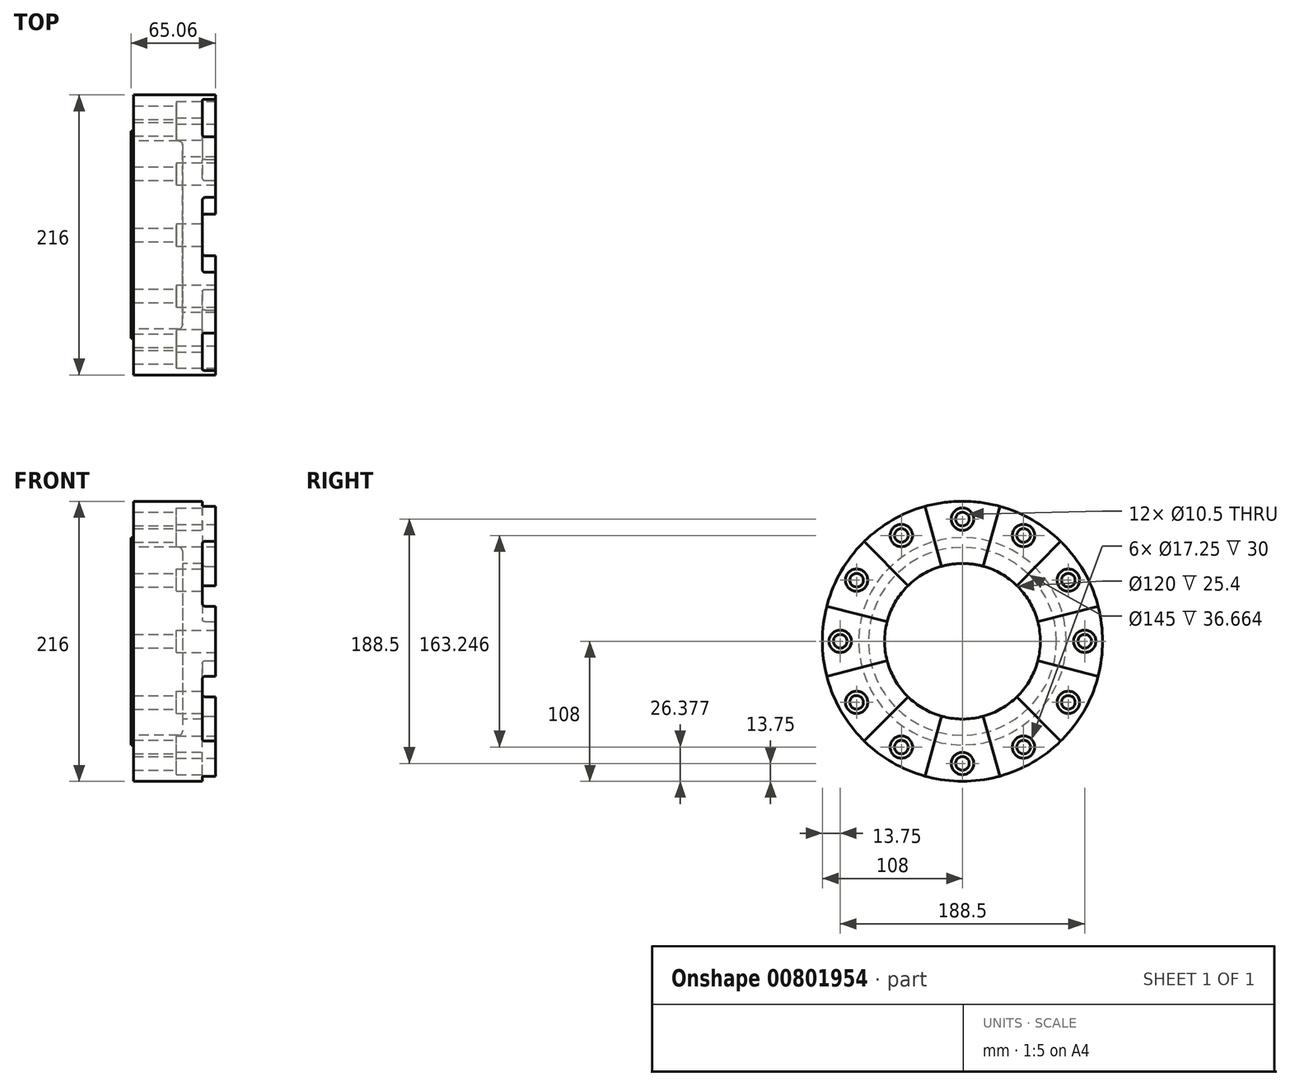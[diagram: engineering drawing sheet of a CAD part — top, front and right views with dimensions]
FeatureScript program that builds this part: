
annotation { "Feature Type Name" : "Feature", "Feature Type Description" : "" }
export const myFeature = defineFeature(function(context is Context, id is Id, definition is map)
    precondition{}
    {
        {
            var Q0;
            Q0=qCreatedBy(makeId("Front.planeOp"),FACE);
            var sketch = newSketch(context, id + "F0", { "sketchPlane" : qUnion([Q0])});
            skLineSegment(sketch, "E0", {"start": v(0, 0) * mm, "end": v(87.54, 0) * mm, "construction": true});
            skLineSegment(sketch, "E1", {"start": v(79.56, 108) * mm, "end": v(79.56, 60) * mm});
            skLineSegment(sketch, "E2", {"start": v(79.56, 60) * mm, "end": v(54.16, 60) * mm});
            skLineSegment(sketch, "E3", {"start": v(54.16, 60) * mm, "end": v(54.16, 69.5) * mm});
            skPoint(sketch, "E4.visualSharp", {"position": v(54.16, 72.5) * mm});
            skLineSegment(sketch, "E5", {"start": v(16.5, 80) * mm, "end": v(16.5, 108) * mm});
            skLineSegment(sketch, "E6", {"start": v(16.5, 108) * mm, "end": v(79.56, 108) * mm});
            skLineSegment(sketch, "E7", {"start": v(14.5, 72.5) * mm, "end": v(14.5, 80) * mm});
            skLineSegment(sketch, "E8", {"start": v(14.5, 80) * mm, "end": v(16.5, 80) * mm});
            skLineSegment(sketch, "E9", {"start": v(14.5, 72.5) * mm, "end": v(51.16, 72.5) * mm});
            skArc(sketch, "E10.filletArc", {"start": v(54.16, 69.5) * mm, "mid": v(53.29, 71.62) * mm, "end": v(51.16, 72.5) * mm});
            skSolve(sketch);
        }
        {
            var Q0;
            Q0=qSketchRegion(id+"F0",true);
            var Q1;
            Q1=sQuery(id+"F0.wireOp",EDGE,"E0");
            revolve(context, id + "F1", {"entities" : qUnion([Q0]), "axis" : qUnion([Q1]), "revolveType" : RevolveType.FULL});
        }
        {
            var Q0;
            Q0=makeQuery(id+"F1.opRevolve","SWEPT_FACE",FACE,{"disambiguationData":[OSD([sQuery(id+"F0.wireOp",EDGE,"E1")])]});
            var sketch = newSketch(context, id + "F2", { "sketchPlane" : qUnion([Q0])});
            skLineSegment(sketch, "E11", {"start": v(0, 0) * mm, "end": v(0, 110.4) * mm, "construction": true});
            skArc(sketch, "E12", {"start": v(-16.03, 57.82) * mm, "mid": v(0, 60) * mm, "end": v(16.03, 57.82) * mm});
            skArc(sketch, "E13", {"start": v(-28.86, 104.07) * mm, "mid": v(0, 108) * mm, "end": v(28.86, 104.07) * mm});
            skLineSegment(sketch, "E14", {"start": v(-28.86, 104.07) * mm, "end": v(-16.03, 57.82) * mm});
            skLineSegment(sketch, "E15", {"start": v(28.86, 104.07) * mm, "end": v(16.03, 57.82) * mm});
            skLineSegment(sketch, "E16.1.0", {"start": v(-75.7, 77.03) * mm, "end": v(-42.05, 42.8) * mm});
            skArc(sketch, "E16.1.1", {"start": v(-58.09, 15.02) * mm, "mid": v(-51.96, 30) * mm, "end": v(-42.05, 42.8) * mm});
            skArc(sketch, "E16.1.2", {"start": v(-104.56, 27.04) * mm, "mid": v(-93.53, 54) * mm, "end": v(-75.7, 77.03) * mm});
            skLineSegment(sketch, "E16.1.3", {"start": v(-104.56, 27.04) * mm, "end": v(-58.09, 15.02) * mm});
            skLineSegment(sketch, "E16.2.0", {"start": v(-104.56, -27.04) * mm, "end": v(-58.09, -15.02) * mm});
            skArc(sketch, "E16.2.1", {"start": v(-42.05, -42.8) * mm, "mid": v(-51.96, -30) * mm, "end": v(-58.09, -15.02) * mm});
            skArc(sketch, "E16.2.2", {"start": v(-75.7, -77.03) * mm, "mid": v(-93.53, -54) * mm, "end": v(-104.56, -27.04) * mm});
            skLineSegment(sketch, "E16.2.3", {"start": v(-75.7, -77.03) * mm, "end": v(-42.05, -42.8) * mm});
            skLineSegment(sketch, "E16.3.0", {"start": v(-28.86, -104.07) * mm, "end": v(-16.03, -57.82) * mm});
            skArc(sketch, "E16.3.1", {"start": v(16.03, -57.82) * mm, "mid": v(0, -60) * mm, "end": v(-16.03, -57.82) * mm});
            skArc(sketch, "E16.3.2", {"start": v(28.86, -104.07) * mm, "mid": v(0, -108) * mm, "end": v(-28.86, -104.07) * mm});
            skLineSegment(sketch, "E16.3.3", {"start": v(28.86, -104.07) * mm, "end": v(16.03, -57.82) * mm});
            skLineSegment(sketch, "E16.4.0", {"start": v(75.7, -77.03) * mm, "end": v(42.05, -42.8) * mm});
            skArc(sketch, "E16.4.1", {"start": v(58.09, -15.02) * mm, "mid": v(51.96, -30) * mm, "end": v(42.05, -42.8) * mm});
            skArc(sketch, "E16.4.2", {"start": v(104.56, -27.04) * mm, "mid": v(93.53, -54) * mm, "end": v(75.7, -77.03) * mm});
            skLineSegment(sketch, "E16.4.3", {"start": v(104.56, -27.04) * mm, "end": v(58.09, -15.02) * mm});
            skLineSegment(sketch, "E16.5.0", {"start": v(104.56, 27.04) * mm, "end": v(58.09, 15.02) * mm});
            skArc(sketch, "E16.5.1", {"start": v(42.05, 42.8) * mm, "mid": v(51.96, 30) * mm, "end": v(58.09, 15.02) * mm});
            skArc(sketch, "E16.5.2", {"start": v(75.7, 77.03) * mm, "mid": v(93.53, 54) * mm, "end": v(104.56, 27.04) * mm});
            skLineSegment(sketch, "E16.5.3", {"start": v(75.7, 77.03) * mm, "end": v(42.05, 42.8) * mm});
            skSolve(sketch);
        }
        {
            var Q0;
            Q0=qSketchRegion(id+"F2",true);
            extrude(context, id + "F3", {"entities" : qUnion([Q0]), "operationType" : NewBodyOperationType.REMOVE, "oppositeDirection" : true, "depth" : 10 * mm});
        }
        {
            var Q0;
            Q0=makeQuery(id+"F3.boolean.opBoolean","SPLIT",FACE,{"disambiguationData":[TD([makeQuery(id+"F3.opExtrude","SWEPT_FACE",FACE,{"disambiguationData":[OSD([sQuery(id+"F2.wireOp",EDGE,"E14")])]})])],"derivedFrom":makeQuery(id+"F1.opRevolve","SWEPT_FACE",FACE,{"disambiguationData":[OSD([sQuery(id+"F0.wireOp",EDGE,"E1")])]})});
            var sketch = newSketch(context, id + "F4", { "sketchPlane" : qUnion([Q0])});
            skLineSegment(sketch, "E17", {"start": v(0, 0) * mm, "end": v(0, 94.25) * mm, "construction": true});
            skCircle(sketch, "E18", {"center": v(0, 94.25) * mm, "radius": 5 * mm});
            skCircle(sketch, "E19.1.0", {"center": v(-47.12, 81.62) * mm, "radius": 5 * mm});
            skCircle(sketch, "E19.2.0", {"center": v(-81.62, 47.13) * mm, "radius": 5 * mm});
            skCircle(sketch, "E19.3.0", {"center": v(-94.25, 0) * mm, "radius": 5 * mm});
            skCircle(sketch, "E19.4.0", {"center": v(-81.62, -47.12) * mm, "radius": 5 * mm});
            skCircle(sketch, "E19.5.0", {"center": v(-47.13, -81.62) * mm, "radius": 5 * mm});
            skCircle(sketch, "E19.6.0", {"center": v(0, -94.25) * mm, "radius": 5 * mm});
            skCircle(sketch, "E19.7.0", {"center": v(47.12, -81.62) * mm, "radius": 5 * mm});
            skCircle(sketch, "E19.8.0", {"center": v(81.62, -47.13) * mm, "radius": 5 * mm});
            skCircle(sketch, "E19.9.0", {"center": v(94.25, 0) * mm, "radius": 5 * mm});
            skCircle(sketch, "E19.10.0", {"center": v(81.62, 47.12) * mm, "radius": 5 * mm});
            skCircle(sketch, "E19.11.0", {"center": v(47.12, 81.62) * mm, "radius": 5 * mm});
            skPoint(sketch, "E19.center", {"position": v(0, 0) * mm});
            skCircle(sketch, "E20", {"center": v(0, 0) * mm, "radius": 94.25 * mm, "construction": true});
            skSolve(sketch);
        }
        {
            var Q0;
            Q0=sQuery(id+"F4.wireOp",VERTEX,"E19.1.0.center");
            var Q1;
            Q1=sQuery(id+"F4.wireOp",VERTEX,"E19.3.0.center");
            var Q2;
            Q2=sQuery(id+"F4.wireOp",VERTEX,"E19.5.0.center");
            var Q3;
            Q3=sQuery(id+"F4.wireOp",VERTEX,"E19.11.0.center");
            var Q4;
            Q4=sQuery(id+"F4.wireOp",VERTEX,"E19.9.0.center");
            var Q5;
            Q5=sQuery(id+"F4.wireOp",VERTEX,"E19.7.0.center");
            var Q6;
            Q6=makeQuery(id+"F1.opRevolve","SWEPT_BODY",BODY,{"disambiguationData":[OSD([sQuery(id+"F0.wireOp",EDGE,"cKsjdh96-D89g-5p2D-h3XL-UVhXMyCSQNq4"),sQuery(id+"F0.wireOp",EDGE,"apuWihD5-RSD5-dsa5-vE7C-J3piarLAXm6q"),sQuery(id+"F0.wireOp",EDGE,"KV8aVnY1-u6Om-Dk3w-krVR-1GxTJCxTkb02"),sQuery(id+"F0.wireOp",EDGE,"Kmc8ooil-dtvY-6vtC-WxYi-Np3pAdkpifhF"),sQuery(id+"F0.wireOp",EDGE,"9beadaba-26b4-418a-b517-611681b9f9d4.filletArc"),sQuery(id+"F0.wireOp",EDGE,"E1"),sQuery(id+"F0.wireOp",EDGE,"E2"),sQuery(id+"F0.wireOp",EDGE,"E3"),sQuery(id+"F0.wireOp",EDGE,"DEHAbUA3-ssQc-y9Ke-qyxT-0Mpok7RH61FX"),sQuery(id+"F0.wireOp",EDGE,"E4.filletArc")])]});
            hole(context, id + "F5", {"style" : HoleStyle.C_BORE, "endStyle" : HoleEndStyle.THROUGH, "holeDiameter" : 10.5 * mm, "cBoreDiameter" : 17.25 * mm, "cBoreDepth" : 30 * mm, "majorDiameter" : 5 * mm, "tappedDepth" : 12 * mm, "tapClearance" : 3, "startFromSketch" : true, "locations" : qUnion([Q0, Q1, Q2, Q3, Q4, Q5]), "scope" : qUnion([Q6])});
        }
        {
            var Q0;
            Q0=makeQuery(id+"F3.boolean.opBoolean","COPY",FACE,{"derivedFrom":makeQuery(id+"F3.opExtrude","CAP_FACE",FACE,{"disambiguationData":[OSD([sQuery(id+"F2.wireOp",EDGE,"E12"),sQuery(id+"F2.wireOp",EDGE,"E13"),sQuery(id+"F2.wireOp",EDGE,"E14"),sQuery(id+"F2.wireOp",EDGE,"E15")])],"isStart":false})});
            var sketch = newSketch(context, id + "F6", { "sketchPlane" : qUnion([Q0])});
            skPoint(sketch, "E21", {"position": v(0, 94.25) * mm});
            skPoint(sketch, "E22.1.0", {"position": v(-81.62, 47.12) * mm});
            skPoint(sketch, "E22.2.0", {"position": v(-81.62, -47.12) * mm});
            skPoint(sketch, "E22.3.0", {"position": v(0, -94.25) * mm});
            skPoint(sketch, "E22.4.0", {"position": v(81.62, -47.13) * mm});
            skPoint(sketch, "E22.5.0", {"position": v(81.62, 47.12) * mm});
            skPoint(sketch, "E22.center", {"position": v(0, 0) * mm});
            skSolve(sketch);
        }
        {
            var Q0;
            Q0=sQuery(id+"F6.wireOp",VERTEX,"E21");
            var Q1;
            Q1=sQuery(id+"F6.wireOp",VERTEX,"E22.1.0");
            var Q2;
            Q2=sQuery(id+"F6.wireOp",VERTEX,"E22.2.0");
            var Q3;
            Q3=sQuery(id+"F6.wireOp",VERTEX,"E22.3.0");
            var Q4;
            Q4=sQuery(id+"F6.wireOp",VERTEX,"E22.4.0");
            var Q5;
            Q5=sQuery(id+"F6.wireOp",VERTEX,"E22.5.0");
            var Q6;
            Q6=makeQuery(id+"F1.opRevolve","SWEPT_BODY",BODY,{"disambiguationData":[OSD([sQuery(id+"F0.wireOp",EDGE,"cKsjdh96-D89g-5p2D-h3XL-UVhXMyCSQNq4"),sQuery(id+"F0.wireOp",EDGE,"apuWihD5-RSD5-dsa5-vE7C-J3piarLAXm6q"),sQuery(id+"F0.wireOp",EDGE,"KV8aVnY1-u6Om-Dk3w-krVR-1GxTJCxTkb02"),sQuery(id+"F0.wireOp",EDGE,"Kmc8ooil-dtvY-6vtC-WxYi-Np3pAdkpifhF"),sQuery(id+"F0.wireOp",EDGE,"9beadaba-26b4-418a-b517-611681b9f9d4.filletArc"),sQuery(id+"F0.wireOp",EDGE,"E1"),sQuery(id+"F0.wireOp",EDGE,"E2"),sQuery(id+"F0.wireOp",EDGE,"E3"),sQuery(id+"F0.wireOp",EDGE,"DEHAbUA3-ssQc-y9Ke-qyxT-0Mpok7RH61FX"),sQuery(id+"F0.wireOp",EDGE,"E4.filletArc")])]});
            hole(context, id + "F7", {"style" : HoleStyle.C_BORE, "endStyle" : HoleEndStyle.THROUGH, "holeDiameter" : 10.5 * mm, "cBoreDiameter" : 17.25 * mm, "cBoreDepth" : 20 * mm, "majorDiameter" : 5 * mm, "tappedDepth" : 12 * mm, "tapClearance" : 3, "startFromSketch" : true, "locations" : qUnion([Q0, Q1, Q2, Q3, Q4, Q5]), "scope" : qUnion([Q6])});
        }
        {
            var Q0;
            Q0=makeQuery(id+"F3.boolean.opBoolean","COPY",EDGE,{"derivedFrom":makeQuery(id+"F3.opExtrude","CAP_EDGE",EDGE,{"disambiguationData":[OSD([sQuery(id+"F2.wireOp",EDGE,"E15")])],"isStart":true})});
            var Q1;
            Q1=makeQuery(id+"F3.boolean.opBoolean","COPY",EDGE,{"derivedFrom":makeQuery(id+"F3.opExtrude","CAP_EDGE",EDGE,{"disambiguationData":[OSD([sQuery(id+"F2.wireOp",EDGE,"E15")])],"isStart":false})});
            var Q2;
            Q2=makeQuery(id+"F3.boolean.opBoolean","COPY",EDGE,{"derivedFrom":makeQuery(id+"F3.opExtrude","CAP_EDGE",EDGE,{"disambiguationData":[OSD([sQuery(id+"F2.wireOp",EDGE,"E14")])],"isStart":true})});
            var Q3;
            Q3=makeQuery(id+"F3.boolean.opBoolean","COPY",EDGE,{"derivedFrom":makeQuery(id+"F3.opExtrude","CAP_EDGE",EDGE,{"disambiguationData":[OSD([sQuery(id+"F2.wireOp",EDGE,"E16.1.0")])],"isStart":true})});
            var Q4;
            Q4=makeQuery(id+"F3.boolean.opBoolean","COPY",EDGE,{"derivedFrom":makeQuery(id+"F3.opExtrude","CAP_EDGE",EDGE,{"disambiguationData":[OSD([sQuery(id+"F2.wireOp",EDGE,"E16.1.0")])],"isStart":false})});
            var Q5;
            Q5=makeQuery(id+"F3.boolean.opBoolean","COPY",EDGE,{"derivedFrom":makeQuery(id+"F3.opExtrude","CAP_EDGE",EDGE,{"disambiguationData":[OSD([sQuery(id+"F2.wireOp",EDGE,"E16.1.3")])],"isStart":false})});
            var Q6;
            Q6=makeQuery(id+"F3.boolean.opBoolean","COPY",EDGE,{"derivedFrom":makeQuery(id+"F3.opExtrude","CAP_EDGE",EDGE,{"disambiguationData":[OSD([sQuery(id+"F2.wireOp",EDGE,"E16.1.3")])],"isStart":true})});
            var Q7;
            Q7=makeQuery(id+"F3.boolean.opBoolean","COPY",EDGE,{"derivedFrom":makeQuery(id+"F3.opExtrude","CAP_EDGE",EDGE,{"disambiguationData":[OSD([sQuery(id+"F2.wireOp",EDGE,"E16.2.0")])],"isStart":true})});
            var Q8;
            Q8=makeQuery(id+"F3.boolean.opBoolean","COPY",EDGE,{"derivedFrom":makeQuery(id+"F3.opExtrude","CAP_EDGE",EDGE,{"disambiguationData":[OSD([sQuery(id+"F2.wireOp",EDGE,"E16.2.3")])],"isStart":false})});
            var Q9;
            Q9=makeQuery(id+"F3.boolean.opBoolean","COPY",EDGE,{"derivedFrom":makeQuery(id+"F3.opExtrude","CAP_EDGE",EDGE,{"disambiguationData":[OSD([sQuery(id+"F2.wireOp",EDGE,"E16.2.3")])],"isStart":true})});
            var Q10;
            Q10=makeQuery(id+"F3.boolean.opBoolean","COPY",EDGE,{"derivedFrom":makeQuery(id+"F3.opExtrude","CAP_EDGE",EDGE,{"disambiguationData":[OSD([sQuery(id+"F2.wireOp",EDGE,"E16.3.0")])],"isStart":true})});
            var Q11;
            Q11=makeQuery(id+"F3.boolean.opBoolean","COPY",EDGE,{"derivedFrom":makeQuery(id+"F3.opExtrude","CAP_EDGE",EDGE,{"disambiguationData":[OSD([sQuery(id+"F2.wireOp",EDGE,"E16.3.3")])],"isStart":false})});
            var Q12;
            Q12=makeQuery(id+"F3.boolean.opBoolean","COPY",EDGE,{"derivedFrom":makeQuery(id+"F3.opExtrude","CAP_EDGE",EDGE,{"disambiguationData":[OSD([sQuery(id+"F2.wireOp",EDGE,"E16.3.3")])],"isStart":true})});
            var Q13;
            Q13=makeQuery(id+"F3.boolean.opBoolean","COPY",EDGE,{"derivedFrom":makeQuery(id+"F3.opExtrude","CAP_EDGE",EDGE,{"disambiguationData":[OSD([sQuery(id+"F2.wireOp",EDGE,"E16.4.0")])],"isStart":true})});
            var Q14;
            Q14=makeQuery(id+"F3.boolean.opBoolean","COPY",EDGE,{"derivedFrom":makeQuery(id+"F3.opExtrude","CAP_EDGE",EDGE,{"disambiguationData":[OSD([sQuery(id+"F2.wireOp",EDGE,"E16.4.3")])],"isStart":true})});
            var Q15;
            Q15=makeQuery(id+"F3.boolean.opBoolean","COPY",EDGE,{"derivedFrom":makeQuery(id+"F3.opExtrude","CAP_EDGE",EDGE,{"disambiguationData":[OSD([sQuery(id+"F2.wireOp",EDGE,"E16.5.0")])],"isStart":true})});
            var Q16;
            Q16=makeQuery(id+"F3.boolean.opBoolean","COPY",EDGE,{"derivedFrom":makeQuery(id+"F3.opExtrude","CAP_EDGE",EDGE,{"disambiguationData":[OSD([sQuery(id+"F2.wireOp",EDGE,"E16.5.0")])],"isStart":false})});
            var Q17;
            Q17=makeQuery(id+"F3.boolean.opBoolean","COPY",EDGE,{"derivedFrom":makeQuery(id+"F3.opExtrude","CAP_EDGE",EDGE,{"disambiguationData":[OSD([sQuery(id+"F2.wireOp",EDGE,"E16.5.3")])],"isStart":true})});
            var Q18;
            Q18=makeQuery(id+"F3.boolean.opBoolean","COPY",EDGE,{"derivedFrom":makeQuery(id+"F3.opExtrude","CAP_EDGE",EDGE,{"disambiguationData":[OSD([sQuery(id+"F2.wireOp",EDGE,"E16.5.3")])],"isStart":false})});
            var Q19;
            Q19=makeQuery(id+"F3.boolean.opBoolean","COPY",EDGE,{"derivedFrom":makeQuery(id+"F3.opExtrude","CAP_EDGE",EDGE,{"disambiguationData":[OSD([sQuery(id+"F2.wireOp",EDGE,"E14")])],"isStart":false})});
            var Q20;
            Q20=makeQuery(id+"F3.boolean.opBoolean","COPY",EDGE,{"derivedFrom":makeQuery(id+"F3.opExtrude","CAP_EDGE",EDGE,{"disambiguationData":[OSD([sQuery(id+"F2.wireOp",EDGE,"E16.2.0")])],"isStart":false})});
            var Q21;
            Q21=makeQuery(id+"F3.boolean.opBoolean","COPY",EDGE,{"derivedFrom":makeQuery(id+"F3.opExtrude","CAP_EDGE",EDGE,{"disambiguationData":[OSD([sQuery(id+"F2.wireOp",EDGE,"E16.3.0")])],"isStart":false})});
            var Q22;
            Q22=makeQuery(id+"F3.boolean.opBoolean","COPY",EDGE,{"derivedFrom":makeQuery(id+"F3.opExtrude","CAP_EDGE",EDGE,{"disambiguationData":[OSD([sQuery(id+"F2.wireOp",EDGE,"E16.4.3")])],"isStart":false})});
            var Q23;
            Q23=makeQuery(id+"F3.boolean.opBoolean","COPY",EDGE,{"derivedFrom":makeQuery(id+"F3.opExtrude","CAP_EDGE",EDGE,{"disambiguationData":[OSD([sQuery(id+"F2.wireOp",EDGE,"E16.4.0")])],"isStart":false})});
            fillet(context, id + "F8", {"entities" : qUnion([Q0, Q1, Q2, Q3, Q4, Q5, Q6, Q7, Q8, Q9, Q10, Q11, Q12, Q13, Q14, Q15, Q16, Q17, Q18, Q19, Q20, Q21, Q22, Q23]), "radius" : 2 * mm, "tangentPropagation" : true, "allowEdgeOverflow" : false});
        }
    });
